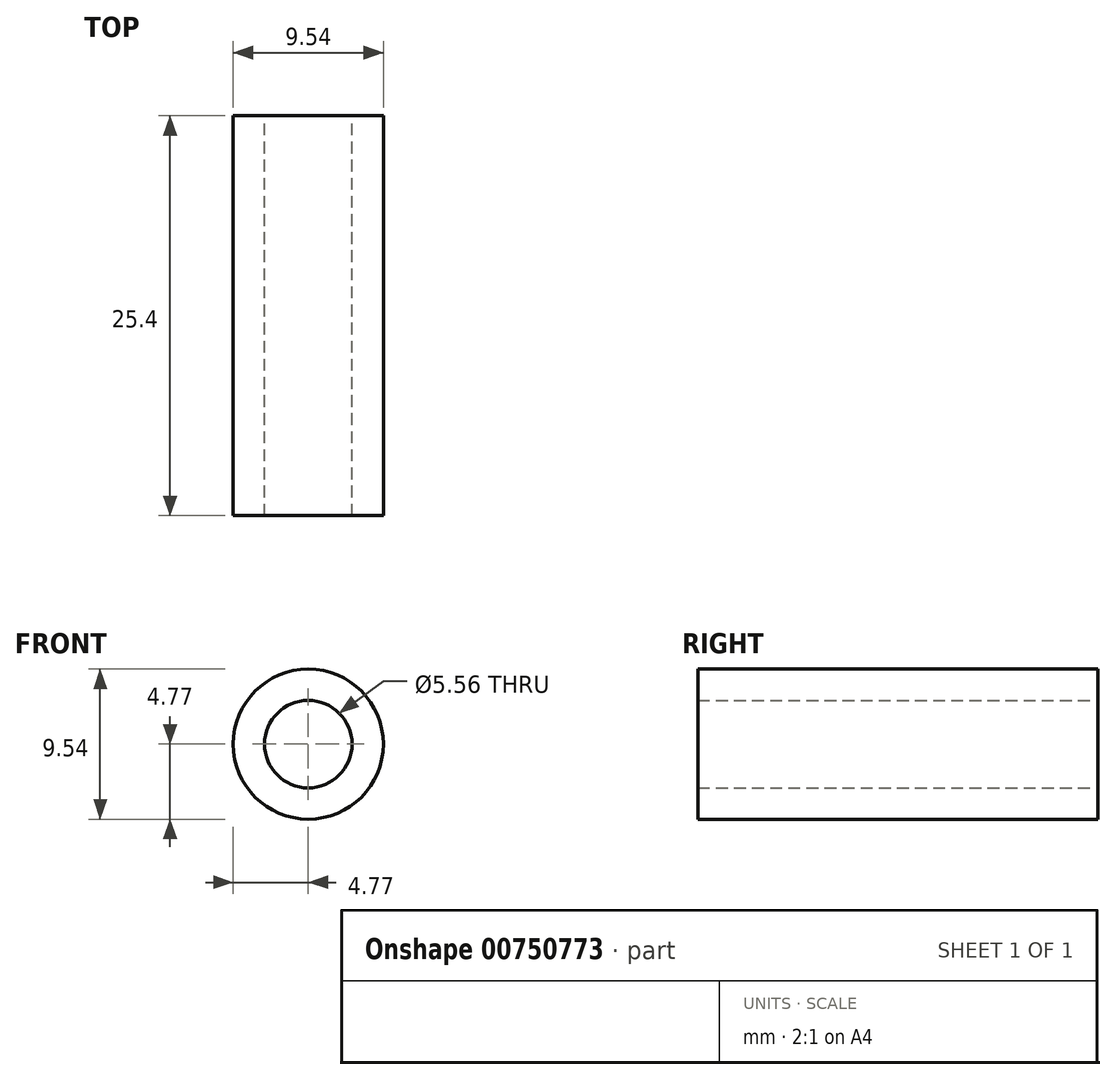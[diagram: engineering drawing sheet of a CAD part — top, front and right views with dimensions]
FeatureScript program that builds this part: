
annotation { "Feature Type Name" : "Feature", "Feature Type Description" : "" }
export const myFeature = defineFeature(function(context is Context, id is Id, definition is map)
    precondition{}
    {
        {
            var Q0;
            Q0=qCreatedBy(makeId("Front.planeOp"),FACE);
            var sketch = newSketch(context, id + "F0", { "sketchPlane" : qUnion([Q0])});
            skCircle(sketch, "E0", {"center": v(0, 0) * mm, "radius": 2.78 * mm});
            skCircle(sketch, "E1", {"center": v(0, 0) * mm, "radius": 4.77 * mm});
            skSolve(sketch);
        }
        {
            var Q0;
            Q0 = qSketchRegion(id + "F0", true);
            extrude(context, id + "F1", {"entities" : qUnion([Q0]), "depth" : 25.4 * mm, "offsetDistance" : 25 * mm});
        }
    });
